# Revit family: Via Seating_Rise_220-45C-11DR-0A1
name_source: partatom
category: Furniture
units: mm (PartAtom-declared; Revit-internal decimal feet)

## family parameters
Always vertical = Yes
Cut with Voids When Loaded = No
OmniClass Number = 23.40.20.00
OmniClass Title = General Furniture and Specialties
Room Calculation Point = No
Shared = No
Work Plane-Based = No

## types (1)
- Via Seating_Rise_220-45C-11DR-0A1
    Description = A very competitive low price point chair that maintains the Via highest standards of quality, durability, comfort, and ergonomics, all delivered within a beautiful, European design cache.  Features include a molded foam seat, fixed and height adjustable arm options, elastomeric mesh in 4 colors, tilt & synchro control mechanisms and a seat depth adjustment.
    Manufacturer = Via Seating
    Model = 220-45C-11DR-0A
    URL = https://viaseating.com

## geometry (parser evidence)
native form markers: Sweep x3
no freeform markers — native parametric forms only
